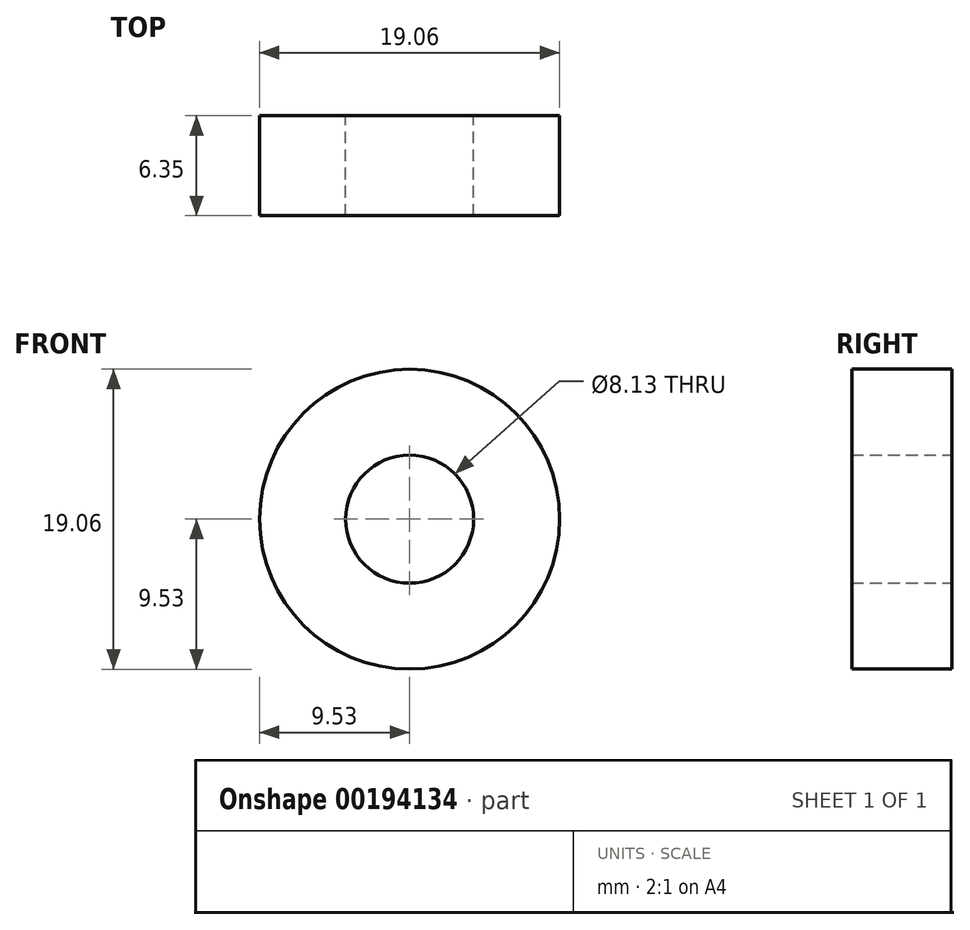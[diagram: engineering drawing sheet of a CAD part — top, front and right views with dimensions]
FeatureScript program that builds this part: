
annotation { "Feature Type Name" : "Feature", "Feature Type Description" : "" }
export const myFeature = defineFeature(function(context is Context, id is Id, definition is map)
    precondition{}
    {
        {
            var Q0;
            Q0=qCreatedBy(makeId("Front.planeOp"),FACE);
            var sketch = newSketch(context, id + "F0", { "sketchPlane" : qUnion([Q0])});
            skCircle(sketch, "E0", {"center": v(0, 0) * mm, "radius": 9.53 * mm});
            skCircle(sketch, "E1", {"center": v(0, 0) * mm, "radius": 4.06 * mm});
            skSolve(sketch);
        }
        {
            var Q0;
            Q0=makeQuery(id+"F0.imprint","IMPRINT",FACE,{"disambiguationData":[TD([[makeQuery(id+"F0.imprint","IMPRINT",EDGE,{"derivedFrom":sQuery(id+"F0.wireOp",EDGE,"E0")}),1.0]])]});
            extrude(context, id + "F1", {"entities" : qUnion([Q0]), "depth" : 6.35 * mm});
        }
    });
